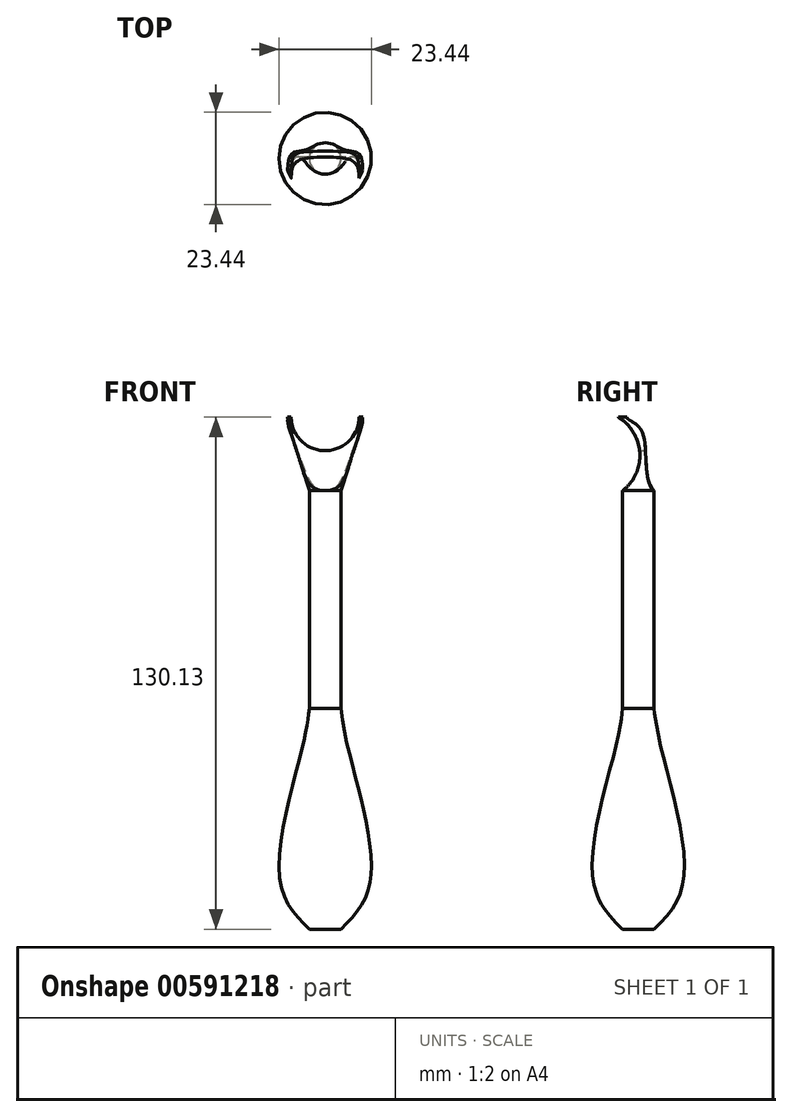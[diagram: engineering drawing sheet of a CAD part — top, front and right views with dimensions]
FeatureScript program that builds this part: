
annotation { "Feature Type Name" : "Feature", "Feature Type Description" : "" }
export const myFeature = defineFeature(function(context is Context, id is Id, definition is map)
    precondition{}
    {
        {
            var Q0;
            Q0=qCreatedBy(makeId("Front.planeOp"),FACE);
            var sketch = newSketch(context, id + "F0", { "sketchPlane" : qUnion([Q0])});
            skLineSegment(sketch, "E0", {"start": v(0, -55.99) * mm, "end": v(0, 74.01) * mm});
            skLineSegment(sketch, "E1", {"start": v(0, 74.01) * mm, "end": v(-10, 74.01) * mm});
            skLineSegment(sketch, "E2", {"start": v(0, 55.3) * mm, "end": v(-4, 55.3) * mm});
            skLineSegment(sketch, "E3", {"start": v(-10, 74.01) * mm, "end": v(-4, 55.3) * mm});
            skLineSegment(sketch, "E4", {"start": v(-4, 55.3) * mm, "end": v(-4, 0) * mm});
            skFitSpline(sketch, "E5", {"points": [v(-4, 0) * mm, v(-5.7, -9.65) * mm, v(-11.55, -43.21) * mm, v(-4, -56.12) * mm], "startDerivative": vector(-3.66, -31.13) * mm, "endDerivative": vector(33.85, -33.54) * mm});
            skLineSegment(sketch, "E6", {"start": v(0, -55.99) * mm, "end": v(-4, -56.12) * mm});
            skSolve(sketch);
        }
        {
            var Q0;
            {var subQ0=sQuery(id+"F0.wireOp",EDGE,"E2");Q0=makeQuery(id+"F0.imprint","IMPRINT",FACE,{"disambiguationData":[TD([[makeQuery(id+"F0.imprint","IMPRINT",EDGE,{"derivedFrom":subQ0}),1.0]])]});}
            var Q1;
            {var subQ0=sQuery(id+"F0.wireOp",EDGE,"E1");Q1=makeQuery(id+"F0.imprint","IMPRINT",FACE,{"disambiguationData":[TD([[makeQuery(id+"F0.imprint","IMPRINT",EDGE,{"derivedFrom":subQ0}),1.0]])]});}
            var Q2;
            Q2=sQuery(id+"F0.wireOp",EDGE,"E0");
            revolve(context, id + "F1", {"entities" : qUnion([Q0, Q1]), "axis" : qUnion([Q2]), "revolveType" : RevolveType.FULL});
        }
        {
            var Q0;
            Q0=qCreatedBy(makeId("Front.planeOp"),FACE);
            var sketch = newSketch(context, id + "F2", { "sketchPlane" : qUnion([Q0])});
            skCircle(sketch, "E7", {"center": v(0, 74.09) * mm, "radius": 8.63 * mm});
            skSolve(sketch);
        }
        {
            var Q0;
            Q0 = qSketchRegion(id + "F2", true);
            extrude(context, id + "F3", {"entities" : qUnion([Q0]), "operationType" : NewBodyOperationType.REMOVE, "endBound" : BoundingType.SYMMETRIC, "oppositeDirection" : true, "depth" : 31.8 * mm, "offsetDistance" : 25 * mm});
        }
        {
            var Q0;
            Q0=qCreatedBy(makeId("Right.planeOp"),FACE);
            var sketch = newSketch(context, id + "F4", { "sketchPlane" : qUnion([Q0])});
            skCircle(sketch, "E8", {"center": v(-9.72, 65.58) * mm, "radius": 9.58 * mm});
            skSolve(sketch);
        }
        {
            var Q0;
            Q0 = qSketchRegion(id + "F4", true);
            extrude(context, id + "F5", {"entities" : qUnion([Q0]), "operationType" : NewBodyOperationType.REMOVE, "endBound" : BoundingType.SYMMETRIC, "oppositeDirection" : true, "depth" : 50.52 * mm, "offsetDistance" : 25 * mm});
        }
        {
            var Q0;
            Q0=qCreatedBy(makeId("Right.planeOp"),FACE);
            var sketch = newSketch(context, id + "F6", { "sketchPlane" : qUnion([Q0])});
            skFitSpline(sketch, "E9", {"points": [v(-2.9, 74.09) * mm, v(0.71, 70.76) * mm, v(4, 55.34) * mm, v(10.23, 55.73) * mm, v(6.58, 59.49) * mm, v(9.95, 66.68) * mm, v(4.93, 76.49) * mm, v(-2.9, 74.09) * mm]});
            skSolve(sketch);
        }
        {
            var Q0;
            Q0 = qSketchRegion(id + "F6", true);
            extrude(context, id + "F7", {"entities" : qUnion([Q0]), "operationType" : NewBodyOperationType.REMOVE, "endBound" : BoundingType.SYMMETRIC, "oppositeDirection" : true, "depth" : 25 * mm, "offsetDistance" : 25 * mm});
        }
        {
            var Q0;
            Q0=qCreatedBy(makeId("Right.planeOp"),FACE);
            var sketch = newSketch(context, id + "F8", { "sketchPlane" : qUnion([Q0])});
            skCircle(sketch, "E10", {"center": v(-10.79, 64.22) * mm, "radius": 11.2 * mm});
            skSolve(sketch);
        }
        {
            var Q0;
            Q0 = qSketchRegion(id + "F8", true);
            extrude(context, id + "F9", {"entities" : qUnion([Q0]), "operationType" : NewBodyOperationType.REMOVE, "endBound" : BoundingType.SYMMETRIC, "oppositeDirection" : true, "depth" : 50.4 * mm, "offsetDistance" : 25 * mm});
        }
    });
